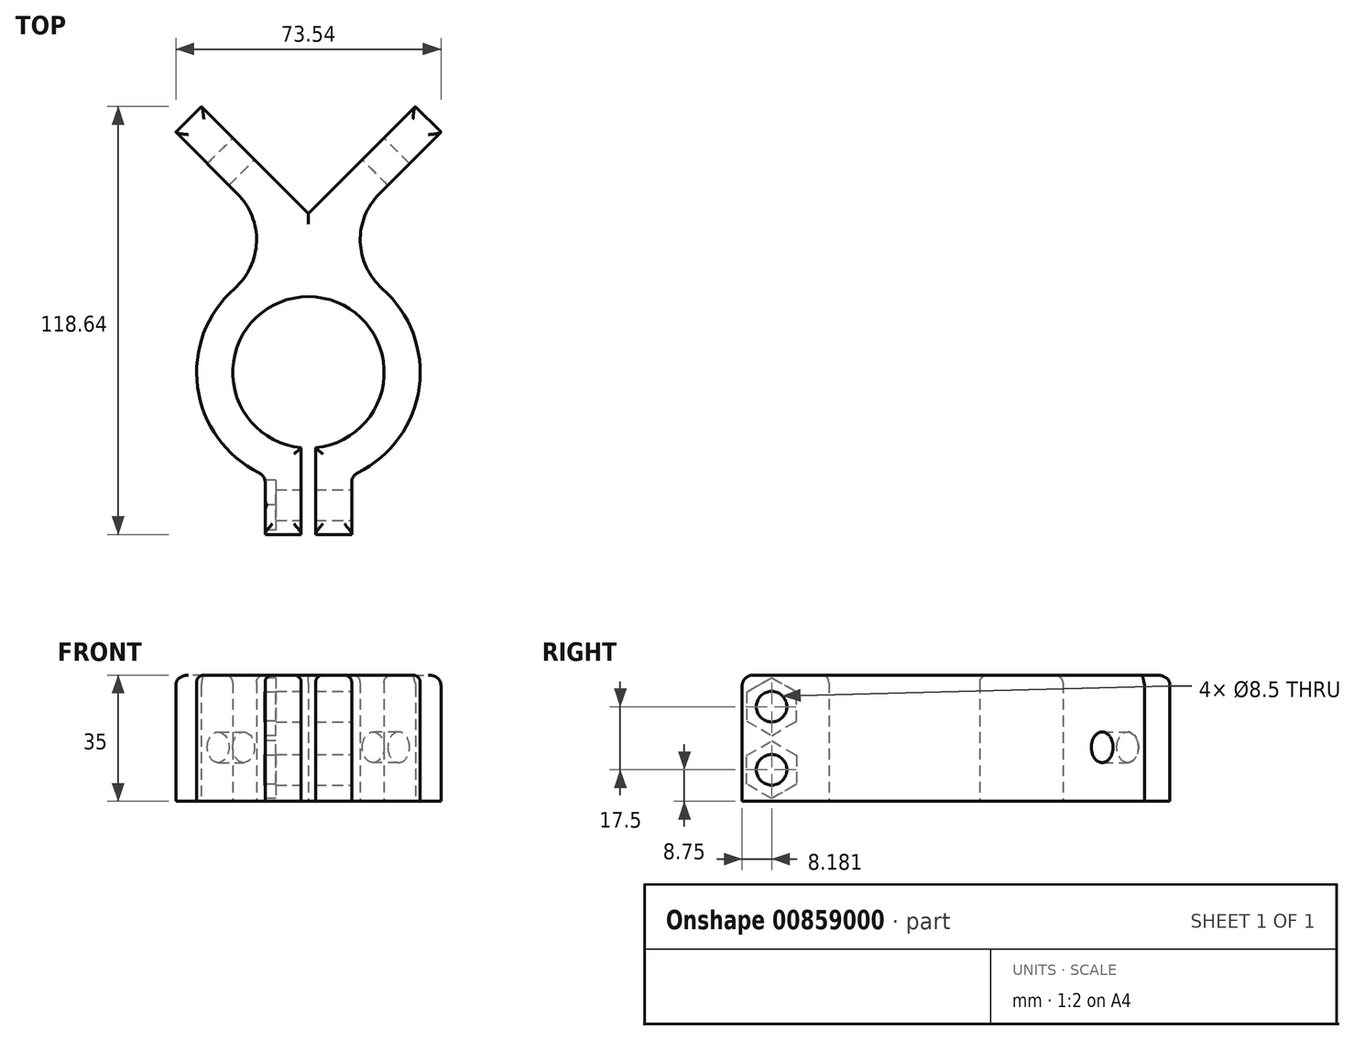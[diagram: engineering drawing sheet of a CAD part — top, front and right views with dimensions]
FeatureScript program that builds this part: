
annotation { "Feature Type Name" : "Feature", "Feature Type Description" : "" }
export const myFeature = defineFeature(function(context is Context, id is Id, definition is map)
    precondition{}
    {
        {
            var Q0;
            Q0=qCreatedBy(makeId("Top.planeOp"),FACE);
            var sketch = newSketch(context, id + "F0", { "sketchPlane" : qUnion([Q0])});
            skLineSegment(sketch, "E0", {"start": v(0, 0) * mm, "end": v(-29.7, 29.7) * mm});
            skLineSegment(sketch, "E1", {"start": v(0, 38.94) * mm, "end": v(0, 0) * mm, "construction": true});
            skLineSegment(sketch, "E2", {"start": v(-29.7, 29.7) * mm, "end": v(-36.77, 22.63) * mm});
            skLineSegment(sketch, "E3", {"start": v(-36.77, 22.63) * mm, "end": v(-1.12, -13.02) * mm});
            skLineSegment(sketch, "E4", {"start": v(0, 0) * mm, "end": v(0, -44) * mm, "construction": true});
            skArc(sketch, "E5", {"start": v(2, -64.9) * mm, "mid": v(0, -23) * mm, "end": v(-2, -64.9) * mm});
            skArc(sketch, "E6", {"start": v(2, -74.94) * mm, "mid": v(31, -43.56) * mm, "end": v(1.12, -13.02) * mm});
            skLineSegment(sketch, "E7", {"start": v(0, -44) * mm, "end": v(0, -75) * mm, "construction": true});
            skLineSegment(sketch, "E8", {"start": v(-2, -74.94) * mm, "end": v(-2, -88.94) * mm});
            skLineSegment(sketch, "E9", {"start": v(-2, -88.94) * mm, "end": v(-12, -88.94) * mm});
            skLineSegment(sketch, "E10", {"start": v(-12, -88.94) * mm, "end": v(-12, -72.58) * mm});
            skLineSegment(sketch, "E11.MirrorCS", {"start": v(2, -88.94) * mm, "end": v(12, -88.94) * mm});
            skLineSegment(sketch, "E12.MirrorCS", {"start": v(12, -88.94) * mm, "end": v(12, -72.58) * mm});
            skLineSegment(sketch, "E13.MirrorCS", {"start": v(2, -74.94) * mm, "end": v(2, -88.94) * mm});
            skLineSegment(sketch, "E14", {"start": v(-2, -74.94) * mm, "end": v(-2, -64.9) * mm});
            skLineSegment(sketch, "E15.MirrorCS", {"start": v(2, -74.94) * mm, "end": v(2, -64.9) * mm});
            skLineSegment(sketch, "E16.MirrorCS", {"start": v(29.7, 29.7) * mm, "end": v(36.77, 22.63) * mm});
            skLineSegment(sketch, "E17.MirrorCS", {"start": v(0, 0) * mm, "end": v(29.7, 29.7) * mm});
            skLineSegment(sketch, "E18.MirrorCS", {"start": v(36.77, 22.63) * mm, "end": v(1.12, -13.02) * mm});
            skPoint(sketch, "E19.orphan", {"position": v(0, -14.14) * mm});
            skArc(sketch, "E20.trimOffspring", {"start": v(-1.12, -13.02) * mm, "mid": v(-31, -43.56) * mm, "end": v(-2, -74.94) * mm});
            skSolve(sketch);
        }
        {
            var Q0;
            Q0=makeQuery(id+"F0.imprint","IMPRINT",FACE,{"disambiguationData":[TD([[makeQuery(id+"F0.imprint","IMPRINT",EDGE,{"derivedFrom":sQuery(id+"F0.wireOp",EDGE,"E0")}),1.0]])]});
            var Q1;
            {var subQ4=sQuery(id+"F0.wireOp",EDGE,"E9");Q1=makeQuery(id+"F0.imprint","IMPRINT",FACE,{"disambiguationData":[TD([[makeQuery(id+"F0.imprint","IMPRINT",EDGE,{"derivedFrom":subQ4}),-1.0]])]});}
            var Q2;
            {var subQ1=sQuery(id+"F0.wireOp",EDGE,"E11.MirrorCS");Q2=makeQuery(id+"F0.imprint","IMPRINT",FACE,{"disambiguationData":[TD([[makeQuery(id+"F0.imprint","IMPRINT",EDGE,{"derivedFrom":subQ1}),1.0]])]});}
            extrude(context, id + "F1", {"entities" : qUnion([Q0, Q1, Q2]), "depth" : 35 * mm, "offsetDistance" : 25 * mm});
        }
        {
            var Q0;
            Q0=makeQuery(id+"F1.opExtrude","SWEPT_FACE",FACE,{"disambiguationData":[OSD([sQuery(id+"F0.wireOp",EDGE,"E17.MirrorCS")])]});
            var sketch = newSketch(context, id + "F2", { "sketchPlane" : qUnion([Q0])});
            skLineSegment(sketch, "E21", {"start": v(0, 15) * mm, "end": v(-50.8, 15) * mm, "construction": true});
            skCircle(sketch, "E22", {"center": v(-25.4, 15) * mm, "radius": 4.25 * mm});
            skSolve(sketch);
        }
        {
            var Q0;
            Q0=qSketchRegion(id+"F2",true);
            extrude(context, id + "F3", {"entities" : qUnion([Q0]), "operationType" : NewBodyOperationType.REMOVE, "endBound" : BoundingType.UP_TO_NEXT, "oppositeDirection" : true, "depth" : 25 * mm, "offsetDistance" : 25 * mm});
        }
        {
            var Q0;
            Q0=makeQuery(id+"F1.opExtrude","SWEPT_FACE",FACE,{"disambiguationData":[OSD([sQuery(id+"F0.wireOp",EDGE,"E0")])]});
            var sketch = newSketch(context, id + "F4", { "sketchPlane" : qUnion([Q0])});
            skLineSegment(sketch, "E23", {"start": v(0, 15) * mm, "end": v(50.8, 15) * mm, "construction": true});
            skCircle(sketch, "E24", {"center": v(25.4, 15) * mm, "radius": 4.25 * mm});
            skSolve(sketch);
        }
        {
            var Q0;
            Q0=qSketchRegion(id+"F4",true);
            extrude(context, id + "F5", {"entities" : qUnion([Q0]), "operationType" : NewBodyOperationType.REMOVE, "endBound" : BoundingType.UP_TO_NEXT, "oppositeDirection" : true, "depth" : 25 * mm, "offsetDistance" : 25 * mm});
        }
        {
            var Q0;
            Q0=makeQuery(id+"F1.opExtrude","SWEPT_FACE",FACE,{"disambiguationData":[OSD([sQuery(id+"F0.wireOp",EDGE,"E12.MirrorCS")])]});
            var sketch = newSketch(context, id + "F6", { "sketchPlane" : qUnion([Q0])});
            skLineSegment(sketch, "E25", {"start": v(-80.76, 35) * mm, "end": v(-80.76, 0) * mm, "construction": true});
            skLineSegment(sketch, "E26", {"start": v(-88.94, 17.5) * mm, "end": v(-72.58, 17.5) * mm, "construction": true});
            skLineSegment(sketch, "E27", {"start": v(-88.94, 17.5) * mm, "end": v(-72.58, 35) * mm, "construction": true});
            skCircle(sketch, "E28", {"center": v(-80.76, 26.25) * mm, "radius": 4.25 * mm});
            skCircle(sketch, "E29.MirrorC", {"center": v(-80.76, 8.75) * mm, "radius": 4.25 * mm});
            skLineSegment(sketch, "E30.MirrorCS", {"start": v(-88.94, 17.5) * mm, "end": v(-72.58, 0) * mm, "construction": true});
            skSolve(sketch);
        }
        {
            var Q0;
            Q0=qSketchRegion(id+"F6",true);
            var Q1;
            Q1=makeQuery(id+"F1.opExtrude","SWEPT_FACE",FACE,{"disambiguationData":[OSD([sQuery(id+"F0.wireOp",EDGE,"E10")])]});
            extrude(context, id + "F7", {"entities" : qUnion([Q0]), "operationType" : NewBodyOperationType.REMOVE, "endBound" : BoundingType.UP_TO_SURFACE, "oppositeDirection" : true, "depth" : 25 * mm, "endBoundEntityFace" : qUnion([Q1]), "offsetDistance" : 25 * mm});
        }
        {
            var Q0;
            Q0=makeQuery(id+"F1.opExtrude","SWEPT_FACE",FACE,{"disambiguationData":[OSD([sQuery(id+"F0.wireOp",EDGE,"E10")])]});
            var sketch = newSketch(context, id + "F8", { "sketchPlane" : qUnion([Q0])});
            skCircle(sketch, "E31.cCircle", {"center": v(80.76, 26.25) * mm, "radius": 6.92 * mm, "construction": true});
            skLineSegment(sketch, "E31.0", {"start": v(80.76, 34.25) * mm, "end": v(87.68, 30.25) * mm});
            skLineSegment(sketch, "E31.1", {"start": v(87.68, 30.25) * mm, "end": v(87.68, 22.25) * mm});
            skLineSegment(sketch, "E31.2", {"start": v(87.68, 22.25) * mm, "end": v(80.76, 18.25) * mm});
            skLineSegment(sketch, "E31.3", {"start": v(80.76, 18.25) * mm, "end": v(73.83, 22.25) * mm});
            skLineSegment(sketch, "E31.4", {"start": v(73.83, 22.25) * mm, "end": v(73.83, 30.25) * mm});
            skLineSegment(sketch, "E31.5", {"start": v(73.83, 30.25) * mm, "end": v(80.76, 34.25) * mm});
            skPoint(sketch, "E31.0.midPoint", {"position": v(84.22, 32.25) * mm});
            skLineSegment(sketch, "E32", {"start": v(88.94, 17.5) * mm, "end": v(74.38, 17.5) * mm, "construction": true});
            skLineSegment(sketch, "E33.MirrorCS", {"start": v(87.68, 12.75) * mm, "end": v(80.76, 16.75) * mm});
            skLineSegment(sketch, "E34.MirrorCS", {"start": v(73.83, 12.75) * mm, "end": v(73.83, 4.75) * mm});
            skLineSegment(sketch, "E35.MirrorCS", {"start": v(80.76, 0.75) * mm, "end": v(87.68, 4.75) * mm});
            skLineSegment(sketch, "E36.MirrorCS", {"start": v(80.76, 16.75) * mm, "end": v(73.83, 12.75) * mm});
            skCircle(sketch, "E37.MirrorC", {"center": v(80.76, 8.75) * mm, "radius": 6.92 * mm, "construction": true});
            skLineSegment(sketch, "E38.MirrorCS", {"start": v(87.68, 4.75) * mm, "end": v(87.68, 12.75) * mm});
            skLineSegment(sketch, "E39.MirrorCS", {"start": v(73.83, 4.75) * mm, "end": v(80.76, 0.75) * mm});
            skPoint(sketch, "E40.MirrorP", {"position": v(84.22, 2.75) * mm});
            skSolve(sketch);
        }
        {
            var Q0;
            Q0=qSketchRegion(id+"F8",true);
            extrude(context, id + "F9", {"entities" : qUnion([Q0]), "operationType" : NewBodyOperationType.REMOVE, "oppositeDirection" : true, "depth" : 3 * mm, "offsetDistance" : 25 * mm});
        }
        {
            var Q0;
            Q0=makeQuery(id+"F1.opExtrude","SWEPT_EDGE",EDGE,{"disambiguationData":[OSD([sQuery(id+"F0.wireOp",EDGE,"E3"),sQuery(id+"F0.wireOp",EDGE,"E20.trimOffspring")])]});
            var Q1;
            Q1=makeQuery(id+"F1.opExtrude","SWEPT_EDGE",EDGE,{"disambiguationData":[OSD([sQuery(id+"F0.wireOp",EDGE,"E6"),sQuery(id+"F0.wireOp",EDGE,"E18.MirrorCS")])]});
            fillet(context, id + "F10", {"entities" : qUnion([Q0, Q1]), "radius" : 18 * mm, "tangentPropagation" : true, "allowEdgeOverflow" : false});
        }
        {
            var Q0;
            Q0=qCreatedBy(makeId("Right.planeOp"),FACE);
            var sketch = newSketch(context, id + "F11", { "sketchPlane" : qUnion([Q0])});
            skLineSegment(sketch, "E41", {"start": v(-80.12, 22.5) * mm, "end": v(-7.68, 22.5) * mm});
            skLineSegment(sketch, "E42", {"start": v(-7.68, 22.5) * mm, "end": v(-7.68, 58.55) * mm});
            skLineSegment(sketch, "E43", {"start": v(-7.68, 58.55) * mm, "end": v(-80.12, 58.55) * mm});
            skLineSegment(sketch, "E44", {"start": v(-80.12, 58.55) * mm, "end": v(-80.12, 22.5) * mm});
            skSolve(sketch);
        }
        {
            var Q0;
            Q0=makeQuery(id+"F1.opExtrude","CAP_EDGE",EDGE,{"disambiguationData":[OSD([sQuery(id+"F0.wireOp",EDGE,"E9")])],"isStart":false});
            var Q1;
            Q1=makeQuery(id+"F1.opExtrude","CAP_EDGE",EDGE,{"disambiguationData":[OSD([sQuery(id+"F0.wireOp",EDGE,"E11.MirrorCS")])],"isStart":false});
            var Q2;
            Q2=makeQuery(id+"F1.opExtrude","CAP_EDGE",EDGE,{"disambiguationData":[OSD([sQuery(id+"F0.wireOp",EDGE,"E2")])],"isStart":false});
            var Q3;
            Q3=makeQuery(id+"F1.opExtrude","CAP_EDGE",EDGE,{"disambiguationData":[OSD([sQuery(id+"F0.wireOp",EDGE,"E16.MirrorCS")])],"isStart":false});
            var Q4;
            Q4=makeQuery(id+"F1.opExtrude","SWEPT_EDGE",EDGE,{"disambiguationData":[OSD([sQuery(id+"F0.wireOp",EDGE,"E10"),sQuery(id+"F0.wireOp",EDGE,"E20.trimOffspring")])]});
            var Q5;
            Q5=makeQuery(id+"F1.opExtrude","SWEPT_EDGE",EDGE,{"disambiguationData":[OSD([sQuery(id+"F0.wireOp",EDGE,"E6"),sQuery(id+"F0.wireOp",EDGE,"E12.MirrorCS")])]});
            var Q6;
            Q6=makeQuery(id+"FpfucTOSUq623gn_1.boolean.opBoolean","INTERSECT",EDGE,{"derivedFrom":[makeQuery(id+"F1.opExtrude","SWEPT_FACE",FACE,{"disambiguationData":[OSD([sQuery(id+"F0.wireOp",EDGE,"E9")])]}),makeQuery(id+"FpfucTOSUq623gn_1.opExtrude","SWEPT_FACE",FACE,{"disambiguationData":[OSD([sQuery(id+"F11.wireOp",EDGE,"E41")])]})]});
            var Q7;
            Q7=makeQuery(id+"FpfucTOSUq623gn_1.boolean.opBoolean","INTERSECT",EDGE,{"derivedFrom":[makeQuery(id+"F1.opExtrude","SWEPT_FACE",FACE,{"disambiguationData":[OSD([sQuery(id+"F0.wireOp",EDGE,"E11.MirrorCS")])]}),makeQuery(id+"FpfucTOSUq623gn_1.opExtrude","SWEPT_FACE",FACE,{"disambiguationData":[OSD([sQuery(id+"F11.wireOp",EDGE,"E41")])]})]});
            fillet(context, id + "F12", {"entities" : qUnion([Q0, Q1, Q2, Q3, Q4, Q5, Q6, Q7]), "radius" : 3 * mm, "tangentPropagation" : true, "allowEdgeOverflow" : false});
        }
        {
            var Q0;
            Q0=makeQuery(id+"F1.opExtrude","CAP_FACE",FACE,{"disambiguationData":[OSD([sQuery(id+"F0.wireOp",EDGE,"E0"),sQuery(id+"F0.wireOp",EDGE,"E2"),sQuery(id+"F0.wireOp",EDGE,"E3"),sQuery(id+"F0.wireOp",EDGE,"E5"),sQuery(id+"F0.wireOp",EDGE,"E6"),sQuery(id+"F0.wireOp",EDGE,"E8"),sQuery(id+"F0.wireOp",EDGE,"E9"),sQuery(id+"F0.wireOp",EDGE,"E10"),sQuery(id+"F0.wireOp",EDGE,"E11.MirrorCS"),sQuery(id+"F0.wireOp",EDGE,"E12.MirrorCS"),sQuery(id+"F0.wireOp",EDGE,"E13.MirrorCS"),sQuery(id+"F0.wireOp",EDGE,"E14"),sQuery(id+"F0.wireOp",EDGE,"E15.MirrorCS"),sQuery(id+"F0.wireOp",EDGE,"E16.MirrorCS"),sQuery(id+"F0.wireOp",EDGE,"E17.MirrorCS"),sQuery(id+"F0.wireOp",EDGE,"E18.MirrorCS"),sQuery(id+"F0.wireOp",EDGE,"E20.trimOffspring")])],"isStart":false});
            fillet(context, id + "F13", {"entities" : qUnion([Q0]), "radius" : 2 * mm, "allowEdgeOverflow" : false});
        }
    });
